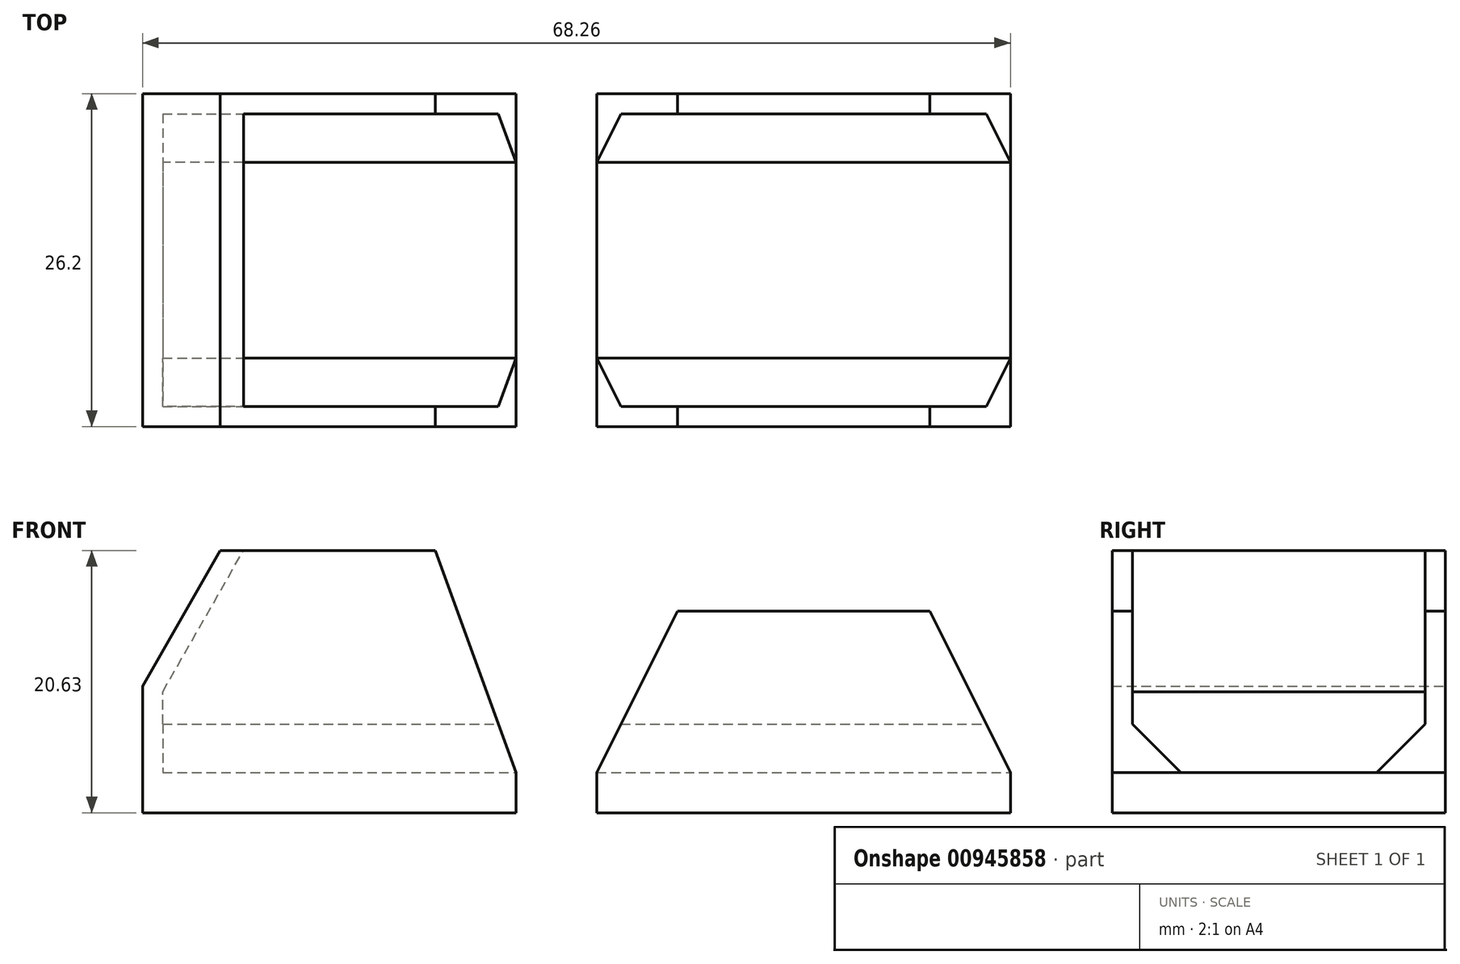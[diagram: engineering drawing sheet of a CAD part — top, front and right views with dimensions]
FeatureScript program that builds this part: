
annotation { "Feature Type Name" : "Feature", "Feature Type Description" : "" }
export const myFeature = defineFeature(function(context is Context, id is Id, definition is map)
    precondition{}
    {
        {
            var Q0;
            Q0=qCreatedBy(makeId("Front.planeOp"),FACE);
            var sketch = newSketch(context, id + "F0", { "sketchPlane" : qUnion([Q0])});
            skLineSegment(sketch, "E0.bottom", {"start": v(41.27, 0) * mm, "end": v(8.73, 0) * mm});
            skLineSegment(sketch, "E0.top", {"start": v(41.27, -3.18) * mm, "end": v(8.73, -3.18) * mm});
            skLineSegment(sketch, "E0.left", {"start": v(41.27, 0) * mm, "end": v(41.27, -3.18) * mm});
            skLineSegment(sketch, "E0.right", {"start": v(8.73, 0) * mm, "end": v(8.73, -3.18) * mm});
            skLineSegment(sketch, "E1", {"start": v(8.73, 0) * mm, "end": v(15.08, 0) * mm});
            skLineSegment(sketch, "E2", {"start": v(15.08, 0) * mm, "end": v(15.08, 12.7) * mm});
            skLineSegment(sketch, "E3", {"start": v(41.27, 0) * mm, "end": v(34.92, 0) * mm});
            skLineSegment(sketch, "E4", {"start": v(34.92, 0) * mm, "end": v(34.92, 12.7) * mm});
            skLineSegment(sketch, "E5", {"start": v(34.92, 12.7) * mm, "end": v(15.08, 12.7) * mm});
            skLineSegment(sketch, "E6", {"start": v(15.08, 12.7) * mm, "end": v(8.73, 0) * mm});
            skLineSegment(sketch, "E7", {"start": v(34.92, 12.7) * mm, "end": v(41.27, 0) * mm});
            skLineSegment(sketch, "E8", {"start": v(8.73, 0) * mm, "end": v(2.38, 0) * mm});
            skLineSegment(sketch, "E9", {"start": v(2.38, 0) * mm, "end": v(2.38, -3.18) * mm});
            skLineSegment(sketch, "E10", {"start": v(2.38, 0) * mm, "end": v(-25.4, 0) * mm});
            skLineSegment(sketch, "E11", {"start": v(-25.4, 0) * mm, "end": v(-25.4, -3.18) * mm});
            skLineSegment(sketch, "E12", {"start": v(-25.4, -3.18) * mm, "end": v(2.38, -3.18) * mm});
            skLineSegment(sketch, "E13", {"start": v(2.38, 0) * mm, "end": v(-3.97, 0) * mm});
            skLineSegment(sketch, "E14", {"start": v(-3.97, 0) * mm, "end": v(-3.97, 17.46) * mm});
            skLineSegment(sketch, "E15", {"start": v(-25.4, 0) * mm, "end": v(-19.05, 0) * mm});
            skLineSegment(sketch, "E16", {"start": v(-19.05, 0) * mm, "end": v(-19.05, 17.46) * mm});
            skLineSegment(sketch, "E17", {"start": v(-19.05, 17.46) * mm, "end": v(-3.97, 17.46) * mm});
            skLineSegment(sketch, "E18", {"start": v(-3.97, 17.46) * mm, "end": v(2.38, 0) * mm});
            skLineSegment(sketch, "E19", {"start": v(-25.4, 0) * mm, "end": v(-25.4, 6.35) * mm});
            skLineSegment(sketch, "E20", {"start": v(-25.4, 6.35) * mm, "end": v(-19.05, 17.46) * mm});
            skLineSegment(sketch, "E21", {"start": v(-25.4, -3.18) * mm, "end": v(-26.99, -3.18) * mm});
            skLineSegment(sketch, "E22", {"start": v(-26.99, -3.18) * mm, "end": v(-26.99, 6.35) * mm});
            skLineSegment(sketch, "E23", {"start": v(-19.06, 20.64) * mm, "end": v(-19.05, 20.64) * mm});
            skLineSegment(sketch, "E24", {"start": v(-26.99, 6.77) * mm, "end": v(-26.99, 6.35) * mm});
            skPoint(sketch, "E25", {"position": v(0, 0) * mm});
            skLineSegment(sketch, "E26", {"start": v(-19.05, 17.46) * mm, "end": v(-20.88, 17.46) * mm});
            skLineSegment(sketch, "E27", {"start": v(-26.99, 6.77) * mm, "end": v(-20.88, 17.46) * mm});
            skSolve(sketch);
        }
        {
            var Q0;
            {var subQ2=sQuery(id+"F0.wireOp",EDGE,"E16");Q0=makeQuery(id+"F0.imprint","IMPRINT",FACE,{"disambiguationData":[TD([[makeQuery(id+"F0.imprint","IMPRINT",EDGE,{"derivedFrom":subQ2}),1.0]])]});}
            var Q1;
            {var subQ2=sQuery(id+"F0.wireOp",EDGE,"E2");Q1=makeQuery(id+"F0.imprint","IMPRINT",FACE,{"disambiguationData":[TD([[makeQuery(id+"F0.imprint","IMPRINT",EDGE,{"derivedFrom":subQ2}),1.0]])]});}
            var Q2;
            {var subQ0=sQuery(id+"F0.wireOp",EDGE,"E4");Q2=makeQuery(id+"F0.imprint","IMPRINT",FACE,{"disambiguationData":[TD([[makeQuery(id+"F0.imprint","IMPRINT",EDGE,{"derivedFrom":subQ0}),-1.0]])]});}
            var Q3;
            {var subQ2=sQuery(id+"F0.wireOp",EDGE,"E14");Q3=makeQuery(id+"F0.imprint","IMPRINT",FACE,{"disambiguationData":[TD([[makeQuery(id+"F0.imprint","IMPRINT",EDGE,{"derivedFrom":subQ2}),-1.0]])]});}
            var Q4;
            Q4=makeQuery(id+"F0.imprint","IMPRINT",FACE,{"disambiguationData":[TD([[makeQuery(id+"F0.imprint","IMPRINT",EDGE,{"derivedFrom":sQuery(id+"F0.wireOp",EDGE,"I7ctIV5r-haUq-msQJ-ciKQ-sJNi5ZSDo7ON")}),1.0]])]});
            var Q5;
            Q5=makeQuery(id+"F0.imprint","IMPRINT",FACE,{"disambiguationData":[TD([[makeQuery(id+"F0.imprint","IMPRINT",EDGE,{"derivedFrom":sQuery(id+"F0.wireOp",EDGE,"qRxDTKWa-go5b-108z-La1Q-J7t4UoFcpPKT")}),-1.0]])]});
            var Q6;
            Q6=makeQuery(id+"F0.imprint","IMPRINT",FACE,{"disambiguationData":[TD([[makeQuery(id+"F0.imprint","IMPRINT",EDGE,{"derivedFrom":sQuery(id+"F0.wireOp",EDGE,"E0.top")}),-1.0]])]});
            var Q7;
            {var subQ2=sQuery(id+"F0.wireOp",EDGE,"E2");Q7=makeQuery(id+"F0.imprint","IMPRINT",FACE,{"disambiguationData":[TD([[makeQuery(id+"F0.imprint","IMPRINT",EDGE,{"derivedFrom":subQ2}),-1.0]])]});}
            var Q8;
            Q8=makeQuery(id+"F0.imprint","IMPRINT",FACE,{"disambiguationData":[TD([[makeQuery(id+"F0.imprint","IMPRINT",EDGE,{"derivedFrom":sQuery(id+"F0.wireOp",EDGE,"K3Ut7JzE-O22b-1SFk-A1nE-N2hGKEiAy60S")}),1.0]])]});
            var Q9;
            Q9=makeQuery(id+"F0.imprint","IMPRINT",FACE,{"disambiguationData":[TD([[makeQuery(id+"F0.imprint","IMPRINT",EDGE,{"derivedFrom":sQuery(id+"F0.wireOp",EDGE,"0fGnaXHx-BxEH-AWF0-0ZZX-LaEMv1kshCxB")}),-1.0]])]});
            var Q10;
            Q10=makeQuery(id+"F0.imprint","IMPRINT",FACE,{"disambiguationData":[TD([[makeQuery(id+"F0.imprint","IMPRINT",EDGE,{"derivedFrom":sQuery(id+"F0.wireOp",EDGE,"E11")}),-1.0]])]});
            var Q11;
            Q11=makeQuery(id+"F0.imprint","IMPRINT",FACE,{"disambiguationData":[TD([[makeQuery(id+"F0.imprint","IMPRINT",EDGE,{"derivedFrom":sQuery(id+"F0.wireOp",EDGE,"E17")}),1.0]])]});
            var Q12;
            {var subQ1=sQuery(id+"F0.wireOp",EDGE,"E9");Q12=makeQuery(id+"F0.imprint","IMPRINT",FACE,{"disambiguationData":[TD([[makeQuery(id+"F0.imprint","IMPRINT",EDGE,{"derivedFrom":subQ1}),-1.0]])]});}
            var Q13;
            {var subQ0=sQuery(id+"F0.wireOp",EDGE,"E14");Q13=makeQuery(id+"F0.imprint","IMPRINT",FACE,{"disambiguationData":[TD([[makeQuery(id+"F0.imprint","IMPRINT",EDGE,{"derivedFrom":subQ0}),1.0]])]});}
            extrude(context, id + "F1", {"entities" : qUnion([Q0, Q1, Q2, Q3, Q4, Q5, Q6, Q7, Q8, Q9, Q10, Q11, Q12, Q13]), "endBound" : BoundingType.SYMMETRIC, "depth" : 26.2 * mm, "offsetDistance" : 25.4 * mm});
        }
        {
            var Q0;
            {var subQ2=sQuery(id+"F0.wireOp",EDGE,"E16");Q0=makeQuery(id+"F0.imprint","IMPRINT",FACE,{"disambiguationData":[TD([[makeQuery(id+"F0.imprint","IMPRINT",EDGE,{"derivedFrom":subQ2}),1.0]])]});}
            var Q1;
            {var subQ0=sQuery(id+"F0.wireOp",EDGE,"E14");Q1=makeQuery(id+"F0.imprint","IMPRINT",FACE,{"disambiguationData":[TD([[makeQuery(id+"F0.imprint","IMPRINT",EDGE,{"derivedFrom":subQ0}),1.0]])]});}
            var Q2;
            {var subQ2=sQuery(id+"F0.wireOp",EDGE,"E14");Q2=makeQuery(id+"F0.imprint","IMPRINT",FACE,{"disambiguationData":[TD([[makeQuery(id+"F0.imprint","IMPRINT",EDGE,{"derivedFrom":subQ2}),-1.0]])]});}
            var Q3;
            {var subQ2=sQuery(id+"F0.wireOp",EDGE,"E2");Q3=makeQuery(id+"F0.imprint","IMPRINT",FACE,{"disambiguationData":[TD([[makeQuery(id+"F0.imprint","IMPRINT",EDGE,{"derivedFrom":subQ2}),-1.0]])]});}
            var Q4;
            {var subQ2=sQuery(id+"F0.wireOp",EDGE,"E2");Q4=makeQuery(id+"F0.imprint","IMPRINT",FACE,{"disambiguationData":[TD([[makeQuery(id+"F0.imprint","IMPRINT",EDGE,{"derivedFrom":subQ2}),1.0]])]});}
            var Q5;
            {var subQ0=sQuery(id+"F0.wireOp",EDGE,"E4");Q5=makeQuery(id+"F0.imprint","IMPRINT",FACE,{"disambiguationData":[TD([[makeQuery(id+"F0.imprint","IMPRINT",EDGE,{"derivedFrom":subQ0}),-1.0]])]});}
            var Q6;
            Q6=makeQuery(id+"F0.imprint","IMPRINT",FACE,{"disambiguationData":[TD([[makeQuery(id+"F0.imprint","IMPRINT",EDGE,{"derivedFrom":sQuery(id+"F0.wireOp",EDGE,"I7ctIV5r-haUq-msQJ-ciKQ-sJNi5ZSDo7ON")}),1.0]])]});
            var Q7;
            Q7=makeQuery(id+"F0.imprint","IMPRINT",FACE,{"disambiguationData":[TD([[makeQuery(id+"F0.imprint","IMPRINT",EDGE,{"derivedFrom":sQuery(id+"F0.wireOp",EDGE,"0fGnaXHx-BxEH-AWF0-0ZZX-LaEMv1kshCxB")}),-1.0]])]});
            var Q8;
            Q8=makeQuery(id+"F0.imprint","IMPRINT",FACE,{"disambiguationData":[TD([[makeQuery(id+"F0.imprint","IMPRINT",EDGE,{"derivedFrom":sQuery(id+"F0.wireOp",EDGE,"qRxDTKWa-go5b-108z-La1Q-J7t4UoFcpPKT")}),-1.0]])]});
            extrude(context, id + "F2", {"entities" : qUnion([Q0, Q1, Q2, Q3, Q4, Q5, Q6, Q7, Q8]), "operationType" : NewBodyOperationType.REMOVE, "endBound" : BoundingType.SYMMETRIC, "oppositeDirection" : true, "depth" : 23.02 * mm, "offsetDistance" : 25.4 * mm});
        }
        {
            var Q0;
            Q0=makeQuery(id+"F2.boolean.opBoolean","COPY",EDGE,{"derivedFrom":makeQuery(id+"F2.opExtrude","CAP_EDGE",EDGE,{"disambiguationData":[OSD([sQuery(id+"F0.wireOp",EDGE,"E10")])],"isStart":true})});
            var Q1;
            Q1=makeQuery(id+"F2.boolean.opBoolean","COPY",EDGE,{"derivedFrom":makeQuery(id+"F2.opExtrude","CAP_EDGE",EDGE,{"disambiguationData":[OSD([sQuery(id+"F0.wireOp",EDGE,"E10")])],"isStart":false})});
            var Q2;
            Q2=makeQuery(id+"F2.boolean.opBoolean","COPY",EDGE,{"derivedFrom":makeQuery(id+"F2.opExtrude","CAP_EDGE",EDGE,{"disambiguationData":[OSD([sQuery(id+"F0.wireOp",EDGE,"E0.bottom")])],"isStart":false})});
            var Q3;
            Q3=makeQuery(id+"F2.boolean.opBoolean","COPY",EDGE,{"derivedFrom":makeQuery(id+"F2.opExtrude","CAP_EDGE",EDGE,{"disambiguationData":[OSD([sQuery(id+"F0.wireOp",EDGE,"0fGnaXHx-BxEH-AWF0-0ZZX-LaEMv1kshCxB"),sQuery(id+"F0.wireOp",EDGE,"I7ctIV5r-haUq-msQJ-ciKQ-sJNi5ZSDo7ON"),sQuery(id+"F0.wireOp",EDGE,"qRxDTKWa-go5b-108z-La1Q-J7t4UoFcpPKT")])],"isStart":false})});
            var Q4;
            Q4=makeQuery(id+"F2.boolean.opBoolean","COPY",EDGE,{"derivedFrom":makeQuery(id+"F2.opExtrude","CAP_EDGE",EDGE,{"disambiguationData":[OSD([sQuery(id+"F0.wireOp",EDGE,"E0.bottom")])],"isStart":true})});
            var Q5;
            Q5=makeQuery(id+"F2.boolean.opBoolean","COPY",EDGE,{"derivedFrom":makeQuery(id+"F2.opExtrude","CAP_EDGE",EDGE,{"disambiguationData":[OSD([sQuery(id+"F0.wireOp",EDGE,"0fGnaXHx-BxEH-AWF0-0ZZX-LaEMv1kshCxB"),sQuery(id+"F0.wireOp",EDGE,"I7ctIV5r-haUq-msQJ-ciKQ-sJNi5ZSDo7ON"),sQuery(id+"F0.wireOp",EDGE,"qRxDTKWa-go5b-108z-La1Q-J7t4UoFcpPKT")])],"isStart":true})});
            chamfer(context, id + "F3", {"entities" : qUnion([Q0, Q1, Q2, Q3, Q4, Q5]), "width" : 3.8 * mm, "tangentPropagation" : true});
        }
    });
